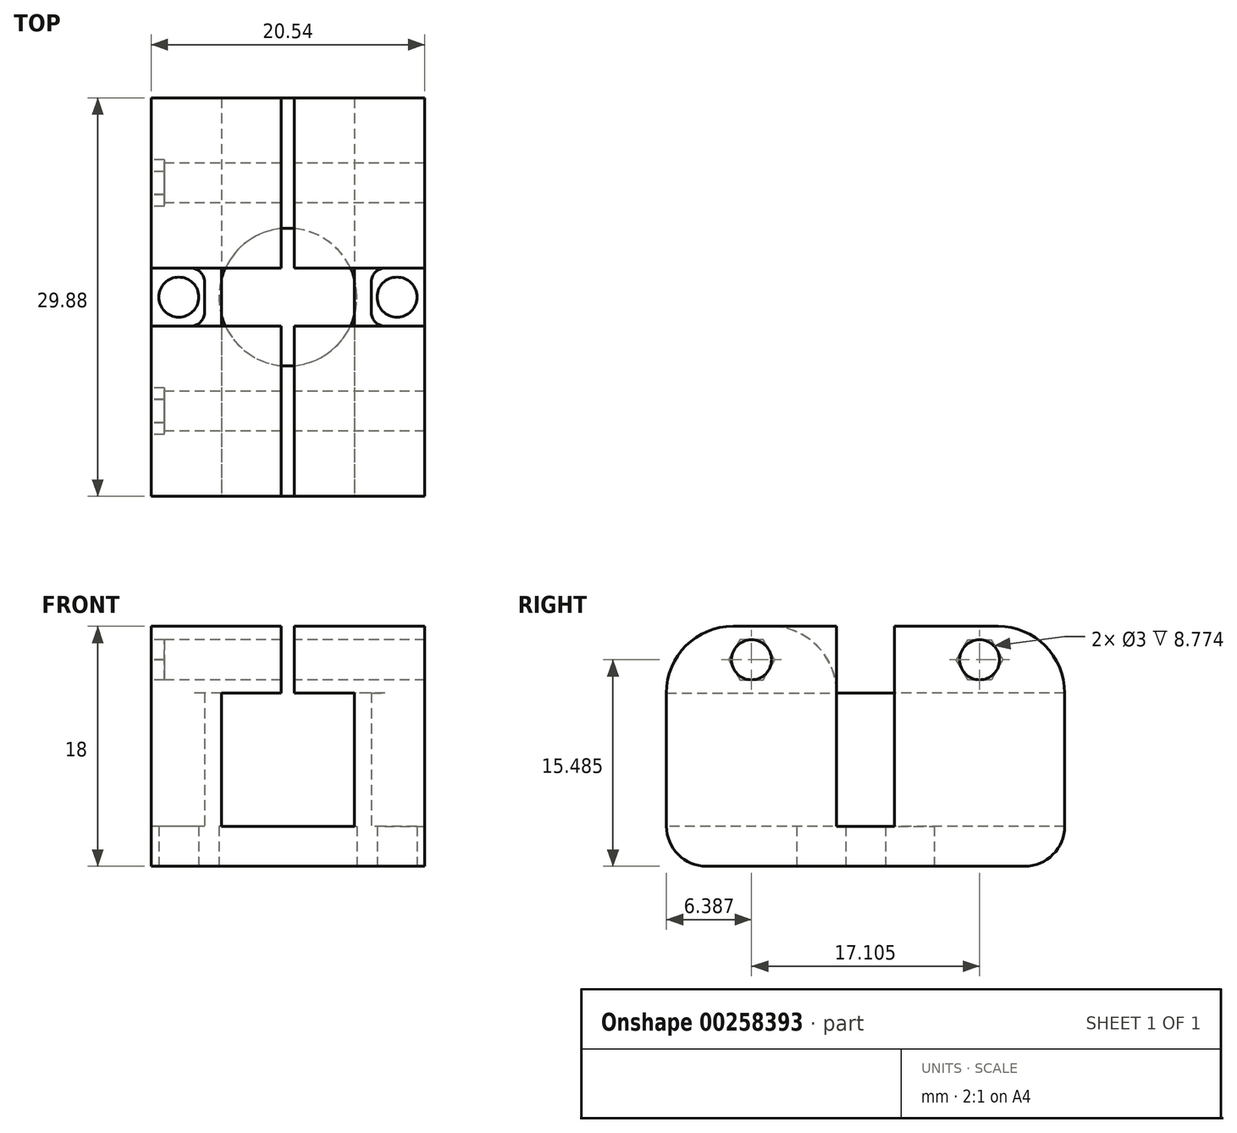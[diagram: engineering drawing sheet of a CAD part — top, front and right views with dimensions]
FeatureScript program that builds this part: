
annotation { "Feature Type Name" : "Feature", "Feature Type Description" : "" }
export const myFeature = defineFeature(function(context is Context, id is Id, definition is map)
    precondition{}
    {
        {
            var Q0;
            Q0=qCreatedBy(makeId("Top.planeOp"),FACE);
            var sketch = newSketch(context, id + "F0", { "sketchPlane" : qUnion([Q0])});
            skPoint(sketch, "E0.middle", {"position": v(0.46, 0) * mm});
            skPoint(sketch, "E1.MirrorC.center.orphan", {"position": v(0.46, 15.48) * mm});
            skPoint(sketch, "E2.center.orphan", {"position": v(12.04, 0) * mm});
            skPoint(sketch, "E3.MirrorC.center.orphan", {"position": v(0.46, -15.48) * mm});
            skPoint(sketch, "E4.MirrorC.center.orphan", {"position": v(-11.12, 0) * mm});
            skLineSegment(sketch, "E5", {"start": v(0, 44.8) * mm, "end": v(0, -39.2) * mm, "construction": true});
            skCircle(sketch, "E6", {"center": v(-8.19, 0) * mm, "radius": 1.5 * mm});
            skCircle(sketch, "E7.MirrorC", {"center": v(8.19, 0) * mm, "radius": 1.5 * mm});
            skCircle(sketch, "E8", {"center": v(0, 0) * mm, "radius": 5.17 * mm});
            skLineSegment(sketch, "E9.bottom", {"start": v(10.27, -14.94) * mm, "end": v(-10.27, -14.94) * mm});
            skLineSegment(sketch, "E9.top", {"start": v(10.27, 14.94) * mm, "end": v(-10.27, 14.94) * mm});
            skLineSegment(sketch, "E9.left", {"start": v(10.27, -14.94) * mm, "end": v(10.27, 14.94) * mm});
            skLineSegment(sketch, "E9.right", {"start": v(-10.27, -14.94) * mm, "end": v(-10.27, 14.94) * mm});
            skPoint(sketch, "E10.MirrorC.center.orphan", {"position": v(0, -12.7) * mm});
            skPoint(sketch, "E11.center.orphan", {"position": v(0, 12.7) * mm});
            skSolve(sketch);
        }
        {
            var Q0;
            Q0=makeQuery(id+"F0.imprint","IMPRINT",FACE,{"disambiguationData":[TD([[makeQuery(id+"F0.imprint","IMPRINT",EDGE,{"derivedFrom":sQuery(id+"F0.wireOp",EDGE,"E6")}),-1.0]])]});
            extrude(context, id + "F1", {"entities" : qUnion([Q0]), "depth" : 3 * mm});
        }
        {
            var Q0;
            Q0=makeQuery(id+"F1.opExtrude","CAP_FACE",FACE,{"disambiguationData":[OSD([sQuery(id+"F0.wireOp",EDGE,"E11"),sQuery(id+"F0.wireOp",EDGE,"E10.MirrorC"),sQuery(id+"F0.wireOp",EDGE,"E6"),sQuery(id+"F0.wireOp",EDGE,"E7.MirrorC"),sQuery(id+"F0.wireOp",EDGE,"E8"),sQuery(id+"F0.wireOp",EDGE,"E9.bottom"),sQuery(id+"F0.wireOp",EDGE,"E9.top"),sQuery(id+"F0.wireOp",EDGE,"E9.left"),sQuery(id+"F0.wireOp",EDGE,"E9.right")])],"isStart":false});
            var sketch = newSketch(context, id + "F2", { "sketchPlane" : qUnion([Q0])});
            skLineSegment(sketch, "E12.bottom", {"start": v(-10.27, 14.94) * mm, "end": v(10.27, 14.94) * mm});
            skLineSegment(sketch, "E12.top", {"start": v(-10.27, 6.67) * mm, "end": v(10.27, 6.67) * mm});
            skLineSegment(sketch, "E12.left", {"start": v(-10.27, 14.94) * mm, "end": v(-10.27, 6.67) * mm});
            skLineSegment(sketch, "E12.right", {"start": v(10.27, 14.94) * mm, "end": v(10.27, 6.67) * mm});
            skLineSegment(sketch, "E13.MirrorCS", {"start": v(-10.27, -6.67) * mm, "end": v(10.27, -6.67) * mm});
            skLineSegment(sketch, "E14.MirrorCS", {"start": v(-10.27, -14.94) * mm, "end": v(10.27, -14.94) * mm});
            skLineSegment(sketch, "E15.MirrorCS", {"start": v(-10.27, -14.94) * mm, "end": v(-10.27, -6.67) * mm});
            skLineSegment(sketch, "E16.MirrorCS", {"start": v(10.27, -14.94) * mm, "end": v(10.27, -6.67) * mm});
            skSolve(sketch);
        }
        {
            var Q0;
            Q0 = qSketchRegion(id + "F2", true);
            extrude(context, id + "F3", {"entities" : qUnion([Q0]), "operationType" : NewBodyOperationType.ADD, "depth" : 15 * mm});
        }
        {
            var Q0;
            Q0=makeQuery(id+"F3.boolean.opBoolean","MERGE",FACE,{"derivedFrom":[makeQuery(id+"F1.opExtrude","SWEPT_FACE",FACE,{"disambiguationData":[OSD([sQuery(id+"F0.wireOp",EDGE,"E9.bottom")])]}),makeQuery(id+"F3.opExtrude","SWEPT_FACE",FACE,{"disambiguationData":[OSD([sQuery(id+"F2.wireOp",EDGE,"E14.MirrorCS")])]})]});
            var sketch = newSketch(context, id + "F4", { "sketchPlane" : qUnion([Q0])});
            skLineSegment(sketch, "E17", {"start": v(0, 0) * mm, "end": v(0, 18) * mm, "construction": true});
            skLineSegment(sketch, "E18", {"start": v(10.27, 8) * mm, "end": v(-10.27, 8) * mm, "construction": true});
            skLineSegment(sketch, "E19.bottom", {"start": v(-5, 13) * mm, "end": v(-0.22, 13) * mm});
            skLineSegment(sketch, "E19.top", {"start": v(-5, 3) * mm, "end": v(5, 3) * mm});
            skLineSegment(sketch, "E19.left", {"start": v(-5, 13) * mm, "end": v(-5, 3) * mm});
            skLineSegment(sketch, "E19.right", {"start": v(5, 13) * mm, "end": v(5, 3) * mm});
            skPoint(sketch, "E19.middle", {"position": v(0, 8) * mm});
            skLineSegment(sketch, "E20.trimOffspring", {"start": v(0.22, 13) * mm, "end": v(5, 13) * mm});
            skLineSegment(sketch, "E21", {"start": v(0.22, 13) * mm, "end": v(-0.22, 13) * mm});
            skPoint(sketch, "E22.end.orphan", {"position": v(0.22, 18) * mm});
            skPoint(sketch, "E23.MirrorCS.end.orphan", {"position": v(-0.22, 18) * mm});
            skSolve(sketch);
        }
        {
            var Q0;
            Q0=makeQuery(id+"F7.boolean.opBoolean","MERGE",FACE,{"derivedFrom":[makeQuery(id+"F1.opExtrude","CAP_FACE",FACE,{"disambiguationData":[OSD([sQuery(id+"F0.wireOp",EDGE,"E6"),sQuery(id+"F0.wireOp",EDGE,"E7.MirrorC"),sQuery(id+"F0.wireOp",EDGE,"E8"),sQuery(id+"F0.wireOp",EDGE,"E9.bottom"),sQuery(id+"F0.wireOp",EDGE,"E9.top"),sQuery(id+"F0.wireOp",EDGE,"E9.left"),sQuery(id+"F0.wireOp",EDGE,"E9.right")])],"isStart":false}),makeQuery(id+"F7.opExtrude","SWEPT_FACE",FACE,{"disambiguationData":[OSD([sQuery(id+"F4.wireOp",EDGE,"E19.top")])]})]});
            var sketch = newSketch(context, id + "F5", { "sketchPlane" : qUnion([Q0])});
            skLineSegment(sketch, "E24", {"start": v(-10.27, 6.67) * mm, "end": v(10.27, 6.67) * mm});
            skLineSegment(sketch, "E25", {"start": v(-10.27, -6.67) * mm, "end": v(10.27, -6.67) * mm});
            skLineSegment(sketch, "E26.bottom", {"start": v(-6.26, 2.17) * mm, "end": v(-10.27, 2.17) * mm});
            skLineSegment(sketch, "E26.top", {"start": v(-6.26, -2.17) * mm, "end": v(-10.27, -2.17) * mm});
            skLineSegment(sketch, "E26.left", {"start": v(-6.26, 2.17) * mm, "end": v(-6.26, -2.17) * mm});
            skPoint(sketch, "E26.middle", {"position": v(-12.24, 0) * mm});
            skPoint(sketch, "E27.orphan", {"position": v(-18.22, -2.17) * mm});
            skPoint(sketch, "E28.orphan", {"position": v(-18.22, 2.17) * mm});
            skLineSegment(sketch, "E29.MirrorCS", {"start": v(6.26, -2.17) * mm, "end": v(10.27, -2.17) * mm});
            skLineSegment(sketch, "E30.MirrorCS", {"start": v(6.26, 2.17) * mm, "end": v(6.26, -2.17) * mm});
            skLineSegment(sketch, "E31.MirrorCS", {"start": v(6.26, 2.17) * mm, "end": v(10.27, 2.17) * mm});
            skLineSegment(sketch, "E32", {"start": v(10.27, -2.17) * mm, "end": v(10.27, -6.67) * mm});
            skLineSegment(sketch, "E33", {"start": v(10.27, 2.17) * mm, "end": v(10.27, 6.67) * mm});
            skPoint(sketch, "E34.orphan", {"position": v(12.05, 2.17) * mm});
            skPoint(sketch, "E35.center.orphan", {"position": v(0, 0) * mm});
            skPoint(sketch, "E35.end.orphan", {"position": v(12.05, -2.17) * mm});
            skLineSegment(sketch, "E36.MirrorCS", {"start": v(-10.27, -2.17) * mm, "end": v(-10.27, -6.67) * mm});
            skLineSegment(sketch, "E37.MirrorCS", {"start": v(-10.27, 2.17) * mm, "end": v(-10.27, 6.67) * mm});
            skPoint(sketch, "E38.orphan", {"position": v(-12.05, 2.17) * mm});
            skPoint(sketch, "E39.trimOffspring.start.orphan", {"position": v(-12.05, -2.17) * mm});
            skSolve(sketch);
        }
        {
            var Q0;
            Q0 = qSketchRegion(id + "F5", true);
            extrude(context, id + "F6", {"entities" : qUnion([Q0]), "operationType" : NewBodyOperationType.ADD, "depth" : 15 * mm});
        }
        {
            var Q0;
            Q0=makeQuery(id+"F4.imprint","IMPRINT",FACE,{"disambiguationData":[TD([[makeQuery(id+"F4.imprint","IMPRINT",EDGE,{"derivedFrom":sQuery(id+"F4.wireOp",EDGE,"E19.bottom")}),-1.0]])]});
            extrude(context, id + "F7", {"entities" : qUnion([Q0]), "operationType" : NewBodyOperationType.REMOVE, "oppositeDirection" : true, "depth" : 33.1 * mm});
        }
        {
            var Q0;
            Q0=makeQuery(id+"F1.opExtrude","CAP_EDGE",EDGE,{"disambiguationData":[OSD([sQuery(id+"F0.wireOp",EDGE,"E9.bottom")])],"isStart":true});
            var Q1;
            Q1=makeQuery(id+"F1.opExtrude","CAP_EDGE",EDGE,{"disambiguationData":[OSD([sQuery(id+"F0.wireOp",EDGE,"E9.top")])],"isStart":true});
            fillet(context, id + "F8", {"entities" : qUnion([Q0, Q1]), "radius" : 3 * mm, "tangentPropagation" : true, "allowEdgeOverflow" : false});
        }
        {
            var Q0;
            Q0=makeQuery(id+"F3.boolean.opBoolean","MERGE",FACE,{"derivedFrom":[makeQuery(id+"F1.opExtrude","SWEPT_FACE",FACE,{"disambiguationData":[OSD([sQuery(id+"F0.wireOp",EDGE,"E9.top")])]}),makeQuery(id+"F3.opExtrude","SWEPT_FACE",FACE,{"disambiguationData":[OSD([sQuery(id+"F2.wireOp",EDGE,"E12.bottom")])]})]});
            var sketch = newSketch(context, id + "F9", { "sketchPlane" : qUnion([Q0])});
            skLineSegment(sketch, "E40", {"start": v(0.5, 13) * mm, "end": v(0.5, 18) * mm});
            skLineSegment(sketch, "E41.MirrorCS", {"start": v(-0.5, 13) * mm, "end": v(-0.5, 18) * mm});
            skSolve(sketch);
        }
        {
            var Q0;
            Q0 = qSketchRegion(id + "F9", true);
            var Q1;
            {var subQ0=sQuery(id+"F9.wireOp",EDGE,"E40");Q1=makeQuery(id+"F9.imprint","IMPRINT",FACE,{"disambiguationData":[TD([[makeQuery(id+"F9.imprint","IMPRINT",EDGE,{"derivedFrom":subQ0}),1.0]])]});}
            extrude(context, id + "F10", {"entities" : qUnion([Q0, Q1]), "operationType" : NewBodyOperationType.REMOVE, "oppositeDirection" : true, "depth" : 37.1 * mm});
        }
        {
            var Q0;
            {var subQ0=sQuery(id+"F5.wireOp",EDGE,"E30.MirrorCS");var subQ1=sQuery(id+"F5.wireOp",EDGE,"E29.MirrorCS");var subQ2=sQuery(id+"F2.wireOp",EDGE,"E14.MirrorCS");var subQ3=sQuery(id+"F2.wireOp",EDGE,"E12.right");var subQ4=sQuery(id+"F5.wireOp",EDGE,"E31.MirrorCS");var subQ5=sQuery(id+"F2.wireOp",EDGE,"E16.MirrorCS");var subQ6=sQuery(id+"F2.wireOp",EDGE,"E12.bottom");var subQ7=sQuery(id+"F5.wireOp",EDGE,"E32");var subQ8=sQuery(id+"F5.wireOp",EDGE,"E33");Q0=makeQuery(id+"F10.boolean.opBoolean","SPLIT",FACE,{"disambiguationData":[TD([makeQuery(id+"F1.opExtrude","SWEPT_FACE",FACE,{"disambiguationData":[OSD([sQuery(id+"F0.wireOp",EDGE,"E9.left")])]})])],"derivedFrom":makeQuery(id+"F6.boolean.opBoolean","MERGE",FACE,{"derivedFrom":[makeQuery(id+"F3.opExtrude","CAP_FACE",FACE,{"disambiguationData":[OSD([subQ6,sQuery(id+"F2.wireOp",EDGE,"E12.top"),sQuery(id+"F2.wireOp",EDGE,"E12.left"),subQ3])],"isStart":false}),makeQuery(id+"F3.opExtrude","CAP_FACE",FACE,{"disambiguationData":[OSD([sQuery(id+"F2.wireOp",EDGE,"E13.MirrorCS"),subQ2,sQuery(id+"F2.wireOp",EDGE,"E15.MirrorCS"),subQ5])],"isStart":false}),makeQuery(id+"F6.opExtrude","CAP_FACE",FACE,{"disambiguationData":[OSD([sQuery(id+"F5.wireOp",EDGE,"E24"),sQuery(id+"F5.wireOp",EDGE,"E25"),sQuery(id+"F5.wireOp",EDGE,"E26.bottom"),sQuery(id+"F5.wireOp",EDGE,"E26.top"),sQuery(id+"F5.wireOp",EDGE,"E26.left"),subQ1,subQ0,subQ4,subQ7,subQ8,sQuery(id+"F5.wireOp",EDGE,"E36.MirrorCS"),sQuery(id+"F5.wireOp",EDGE,"E37.MirrorCS")])],"isStart":false})]})});}
            var sketch = newSketch(context, id + "F11", { "sketchPlane" : qUnion([Q0])});
            skLineSegment(sketch, "E42.bottom", {"start": v(6.26, 2.17) * mm, "end": v(-6.26, 2.17) * mm});
            skLineSegment(sketch, "E42.top", {"start": v(6.26, -2.17) * mm, "end": v(-6.26, -2.17) * mm});
            skLineSegment(sketch, "E42.left", {"start": v(6.26, 2.17) * mm, "end": v(6.26, -2.17) * mm});
            skLineSegment(sketch, "E42.right", {"start": v(-6.26, 2.17) * mm, "end": v(-6.26, -2.17) * mm});
            skSolve(sketch);
        }
        {
            var Q0;
            Q0 = qSketchRegion(id + "F11", true);
            extrude(context, id + "F12", {"entities" : qUnion([Q0]), "operationType" : NewBodyOperationType.REMOVE, "oppositeDirection" : true, "depth" : 5 * mm});
        }
        {
            var Q0;
            Q0=makeQuery(id+"F12.boolean.opBoolean","SPLIT",EDGE,{"derivedFrom":makeQuery(id+"F6.opExtrude","SWEPT_EDGE",EDGE,{"disambiguationData":[OSD([sQuery(id+"F5.wireOp",EDGE,"E26.top"),sQuery(id+"F5.wireOp",EDGE,"E26.left")])]})});
            var Q1;
            Q1=makeQuery(id+"F6.opExtrude","SWEPT_EDGE",EDGE,{"disambiguationData":[OSD([sQuery(id+"F5.wireOp",EDGE,"E26.bottom"),sQuery(id+"F5.wireOp",EDGE,"E26.left")])]});
            var Q2;
            Q2=makeQuery(id+"F12.boolean.opBoolean","SPLIT",EDGE,{"derivedFrom":makeQuery(id+"F6.opExtrude","SWEPT_EDGE",EDGE,{"disambiguationData":[OSD([sQuery(id+"F5.wireOp",EDGE,"E29.MirrorCS"),sQuery(id+"F5.wireOp",EDGE,"E30.MirrorCS")])]})});
            var Q3;
            Q3=makeQuery(id+"F6.opExtrude","SWEPT_EDGE",EDGE,{"disambiguationData":[OSD([sQuery(id+"F5.wireOp",EDGE,"E30.MirrorCS"),sQuery(id+"F5.wireOp",EDGE,"E31.MirrorCS")])]});
            fillet(context, id + "F13", {"entities" : qUnion([Q0, Q1, Q2, Q3]), "radius" : 1 * mm, "tangentPropagation" : true, "allowEdgeOverflow" : false});
        }
        {
            var Q0;
            Q0=makeQuery(id+"F6.boolean.opBoolean","MERGE",FACE,{"derivedFrom":[makeQuery(id+"F3.boolean.opBoolean","MERGE",FACE,{"derivedFrom":[makeQuery(id+"F1.opExtrude","SWEPT_FACE",FACE,{"disambiguationData":[OSD([sQuery(id+"F0.wireOp",EDGE,"E9.right")])]}),makeQuery(id+"F3.opExtrude","SWEPT_FACE",FACE,{"disambiguationData":[OSD([sQuery(id+"F2.wireOp",EDGE,"E12.left")])]}),makeQuery(id+"F3.opExtrude","SWEPT_FACE",FACE,{"disambiguationData":[OSD([sQuery(id+"F2.wireOp",EDGE,"E15.MirrorCS")])]})]}),makeQuery(id+"F6.opExtrude","SWEPT_FACE",FACE,{"disambiguationData":[OSD([sQuery(id+"F5.wireOp",EDGE,"E36.MirrorCS")])]}),makeQuery(id+"F6.opExtrude","SWEPT_FACE",FACE,{"disambiguationData":[OSD([sQuery(id+"F5.wireOp",EDGE,"E37.MirrorCS")])]})]});
            var sketch = newSketch(context, id + "F14", { "sketchPlane" : qUnion([Q0])});
            skLineSegment(sketch, "E43", {"start": v(8.55, 18) * mm, "end": v(8.55, 0) * mm, "construction": true});
            skLineSegment(sketch, "E44", {"start": v(-8.55, 18) * mm, "end": v(-8.55, 0) * mm, "construction": true});
            skCircle(sketch, "E45", {"center": v(-8.55, 15.48) * mm, "radius": 1.5 * mm});
            skCircle(sketch, "E46.MirrorC", {"center": v(8.55, 15.48) * mm, "radius": 1.5 * mm});
            skSolve(sketch);
        }
        {
            var Q0;
            Q0 = qSketchRegion(id + "F14", true);
            extrude(context, id + "F15", {"entities" : qUnion([Q0]), "operationType" : NewBodyOperationType.REMOVE, "oppositeDirection" : true, "depth" : 25 * mm});
        }
        {
            var Q0;
            Q0=makeQuery(id+"F6.boolean.opBoolean","MERGE",FACE,{"derivedFrom":[makeQuery(id+"F3.boolean.opBoolean","MERGE",FACE,{"derivedFrom":[makeQuery(id+"F1.opExtrude","SWEPT_FACE",FACE,{"disambiguationData":[OSD([sQuery(id+"F0.wireOp",EDGE,"E9.right")])]}),makeQuery(id+"F3.opExtrude","SWEPT_FACE",FACE,{"disambiguationData":[OSD([sQuery(id+"F2.wireOp",EDGE,"E12.left")])]}),makeQuery(id+"F3.opExtrude","SWEPT_FACE",FACE,{"disambiguationData":[OSD([sQuery(id+"F2.wireOp",EDGE,"E15.MirrorCS")])]})]}),makeQuery(id+"F6.opExtrude","SWEPT_FACE",FACE,{"disambiguationData":[OSD([sQuery(id+"F5.wireOp",EDGE,"E36.MirrorCS")])]}),makeQuery(id+"F6.opExtrude","SWEPT_FACE",FACE,{"disambiguationData":[OSD([sQuery(id+"F5.wireOp",EDGE,"E37.MirrorCS")])]})]});
            var sketch = newSketch(context, id + "F16", { "sketchPlane" : qUnion([Q0])});
            skCircle(sketch, "E47.cCircle", {"center": v(8.55, 15.48) * mm, "radius": 1.5 * mm, "construction": true});
            skLineSegment(sketch, "E47.0", {"start": v(6.81, 15.48) * mm, "end": v(7.68, 16.99) * mm});
            skLineSegment(sketch, "E47.1", {"start": v(7.68, 16.99) * mm, "end": v(9.42, 17) * mm});
            skLineSegment(sketch, "E47.2", {"start": v(9.42, 17) * mm, "end": v(10.3, 15.5) * mm});
            skLineSegment(sketch, "E47.3", {"start": v(10.3, 15.5) * mm, "end": v(9.43, 13.98) * mm});
            skLineSegment(sketch, "E47.4", {"start": v(9.43, 13.98) * mm, "end": v(7.69, 13.97) * mm});
            skLineSegment(sketch, "E47.5", {"start": v(7.69, 13.97) * mm, "end": v(6.81, 15.48) * mm});
            skPoint(sketch, "E47.0.midPoint", {"position": v(7.25, 16.23) * mm});
            skLineSegment(sketch, "E48.MirrorCS", {"start": v(-9.43, 13.98) * mm, "end": v(-7.69, 13.97) * mm});
            skLineSegment(sketch, "E49.MirrorCS", {"start": v(-7.69, 13.97) * mm, "end": v(-6.81, 15.48) * mm});
            skLineSegment(sketch, "E50.MirrorCS", {"start": v(-6.81, 15.48) * mm, "end": v(-7.68, 16.99) * mm});
            skCircle(sketch, "E51.MirrorC", {"center": v(-8.55, 15.48) * mm, "radius": 1.5 * mm, "construction": true});
            skLineSegment(sketch, "E52.MirrorCS", {"start": v(-7.68, 16.99) * mm, "end": v(-9.42, 17) * mm});
            skLineSegment(sketch, "E53.MirrorCS", {"start": v(-9.42, 17) * mm, "end": v(-10.3, 15.5) * mm});
            skLineSegment(sketch, "E54.MirrorCS", {"start": v(-10.3, 15.5) * mm, "end": v(-9.43, 13.98) * mm});
            skSolve(sketch);
        }
        {
            var Q0;
            Q0 = qSketchRegion(id + "F16", true);
            extrude(context, id + "F17", {"entities" : qUnion([Q0]), "operationType" : NewBodyOperationType.REMOVE, "oppositeDirection" : true, "depth" : 1 * mm});
        }
        {
            var Q0;
            {var subQ2=sQuery(id+"F2.wireOp",EDGE,"E14.MirrorCS");Q0=makeQuery(id+"F10.boolean.opBoolean","SPLIT",EDGE,{"disambiguationData":[TD([makeQuery(id+"F1.opExtrude","SWEPT_FACE",FACE,{"disambiguationData":[OSD([sQuery(id+"F0.wireOp",EDGE,"E9.left")])]})])],"derivedFrom":makeQuery(id+"F3.opExtrude","CAP_EDGE",EDGE,{"disambiguationData":[OSD([subQ2])],"isStart":false})});}
            var Q1;
            {var subQ3=sQuery(id+"F2.wireOp",EDGE,"E14.MirrorCS");Q1=makeQuery(id+"F10.boolean.opBoolean","SPLIT",EDGE,{"disambiguationData":[TD([makeQuery(id+"F1.opExtrude","SWEPT_FACE",FACE,{"disambiguationData":[OSD([sQuery(id+"F0.wireOp",EDGE,"E9.right")])]})])],"derivedFrom":makeQuery(id+"F3.opExtrude","CAP_EDGE",EDGE,{"disambiguationData":[OSD([subQ3])],"isStart":false})});}
            var Q2;
            Q2=makeQuery(id+"F6.opExtrude","CAP_EDGE",EDGE,{"disambiguationData":[OSD([sQuery(id+"F5.wireOp",EDGE,"E26.top")])],"isStart":false});
            var Q3;
            {var subQ0=sQuery(id+"F5.wireOp",EDGE,"E29.MirrorCS");var subQ1=sQuery(id+"F11.wireOp",EDGE,"E42.top");Q3=makeQuery(id+"F12.boolean.opBoolean","COPY",EDGE,{"disambiguationData":[TD([makeQuery(id+"F6.opExtrude","SWEPT_FACE",FACE,{"disambiguationData":[OSD([subQ0])]})])],"derivedFrom":makeQuery(id+"F12.opExtrude","CAP_EDGE",EDGE,{"disambiguationData":[OSD([subQ1])],"isStart":true})});}
            var Q4;
            {var subQ4=sQuery(id+"F2.wireOp",EDGE,"E12.bottom");Q4=makeQuery(id+"F10.boolean.opBoolean","SPLIT",EDGE,{"disambiguationData":[TD([makeQuery(id+"F1.opExtrude","SWEPT_FACE",FACE,{"disambiguationData":[OSD([sQuery(id+"F0.wireOp",EDGE,"E9.left")])]})])],"derivedFrom":makeQuery(id+"F3.opExtrude","CAP_EDGE",EDGE,{"disambiguationData":[OSD([subQ4])],"isStart":false})});}
            var Q5;
            Q5=makeQuery(id+"F12.boolean.opBoolean","MERGE",EDGE,{"derivedFrom":[makeQuery(id+"F6.opExtrude","CAP_EDGE",EDGE,{"disambiguationData":[OSD([sQuery(id+"F5.wireOp",EDGE,"E31.MirrorCS")])],"isStart":false}),makeQuery(id+"F12.opExtrude","CAP_EDGE",EDGE,{"disambiguationData":[OSD([sQuery(id+"F11.wireOp",EDGE,"E42.bottom")])],"isStart":true})]});
            var Q6;
            Q6=makeQuery(id+"F12.boolean.opBoolean","MERGE",EDGE,{"derivedFrom":[makeQuery(id+"F6.opExtrude","CAP_EDGE",EDGE,{"disambiguationData":[OSD([sQuery(id+"F5.wireOp",EDGE,"E26.bottom")])],"isStart":false}),makeQuery(id+"F12.opExtrude","CAP_EDGE",EDGE,{"disambiguationData":[OSD([sQuery(id+"F11.wireOp",EDGE,"E42.bottom")])],"isStart":true})]});
            var Q7;
            {var subQ4=sQuery(id+"F2.wireOp",EDGE,"E12.bottom");Q7=makeQuery(id+"F10.boolean.opBoolean","SPLIT",EDGE,{"disambiguationData":[TD([makeQuery(id+"F1.opExtrude","SWEPT_FACE",FACE,{"disambiguationData":[OSD([sQuery(id+"F0.wireOp",EDGE,"E9.right")])]})])],"derivedFrom":makeQuery(id+"F3.opExtrude","CAP_EDGE",EDGE,{"disambiguationData":[OSD([subQ4])],"isStart":false})});}
            fillet(context, id + "F18", {"entities" : qUnion([Q0, Q1, Q2, Q3, Q4, Q5, Q6, Q7]), "radius" : 5 * mm, "tangentPropagation" : true, "allowEdgeOverflow" : false});
        }
    });
